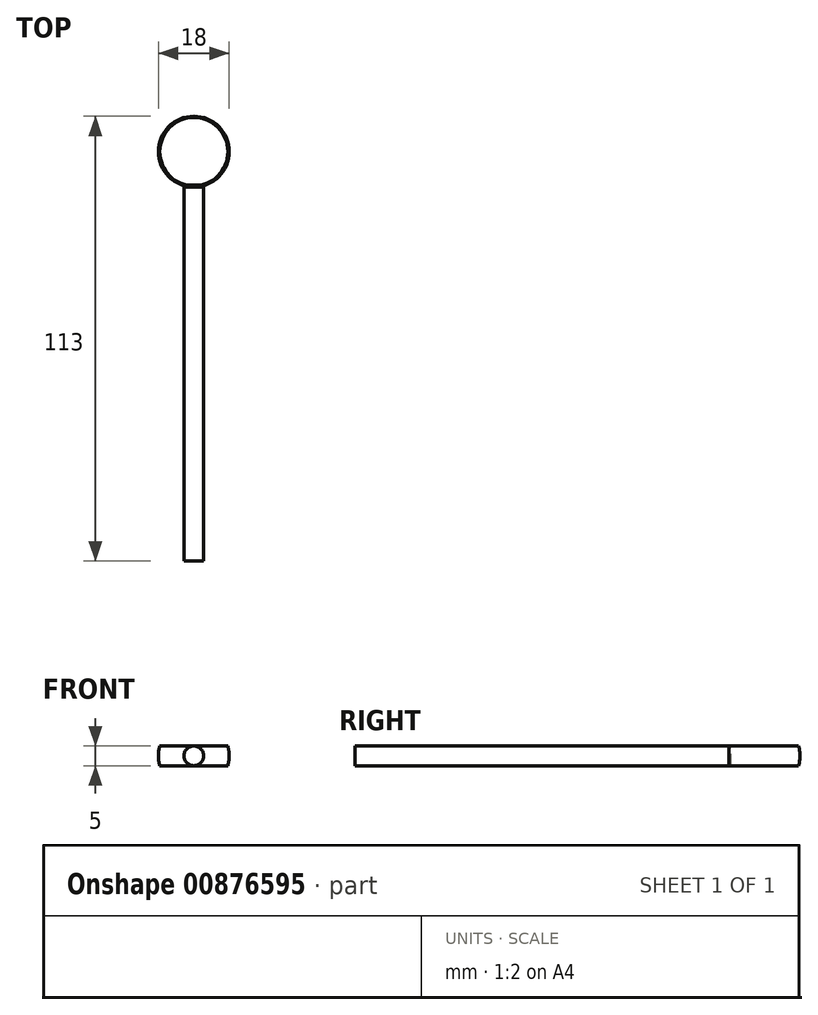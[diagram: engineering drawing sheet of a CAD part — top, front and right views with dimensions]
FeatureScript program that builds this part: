
annotation { "Feature Type Name" : "Feature", "Feature Type Description" : "" }
export const myFeature = defineFeature(function(context is Context, id is Id, definition is map)
    precondition{}
    {
        {
            var Q0;
            Q0=qCreatedBy(makeId("Front.planeOp"),FACE);
            var sketch = newSketch(context, id + "F0", { "sketchPlane" : qUnion([Q0])});
            skCircle(sketch, "E0", {"center": v(0, 0) * mm, "radius": 2.5 * mm});
            skLineSegment(sketch, "E1", {"start": v(0, 2.5) * mm, "end": v(0, -2.5) * mm});
            skSolve(sketch);
        }
        {
            var Q0;
            Q0=makeQuery(id+"F0.imprint","IMPRINT",FACE,{"disambiguationData":[TD([[makeQuery(id+"F0.imprint","IMPRINT",EDGE,{"derivedFrom":sQuery(id+"F0.wireOp",EDGE,"E0")}),1.0]])]});
            extrude(context, id + "F1", {"entities" : qUnion([Q0]), "depth" : 95 * mm, "offsetDistance" : 25 * mm});
        }
        {
            var Q0;
            Q0=sQuery(id+"F0.wireOp",EDGE,"E1");
            extrude(context, id + "F2", {"bodyType" : ToolBodyType.SURFACE, "surfaceEntities" : qUnion([Q0]), "oppositeDirection" : true, "depth" : 9 * mm, "offsetDistance" : 25 * mm});
        }
        {
            var Q0;
            Q0=makeQuery(id+"F2.opExtrude","SWEPT_FACE",FACE,{"disambiguationData":[OSD([sQuery(id+"F0.wireOp",EDGE,"E1")])]});
            var sketch = newSketch(context, id + "F3", { "sketchPlane" : qUnion([Q0])});
            skCircle(sketch, "E2", {"center": v(9, 0) * mm, "radius": 9 * mm});
            skLineSegment(sketch, "E3", {"start": v(9, 0) * mm, "end": v(9, 9) * mm});
            skLineSegment(sketch, "E4", {"start": v(9, 0) * mm, "end": v(9, -9) * mm});
            skLineSegment(sketch, "E5", {"start": v(9, 9) * mm, "end": v(9, -9) * mm});
            skSolve(sketch);
        }
        {
            var Q0;
            {var subQ0=sQuery(id+"F3.wireOp",EDGE,"E5");var subQ1=sQuery(id+"F3.wireOp",EDGE,"E2");var subQ2=makeQuery(id+"F3.imprint","INTERSECT",VERTEX,{"disambiguationData":[OD(0.0)],"derivedFrom":[subQ1,subQ0]});Q0=makeQuery(id+"F3.imprint","IMPRINT",FACE,{"disambiguationData":[TD([[makeQuery(id+"F3.imprint","IMPRINT",EDGE,{"disambiguationData":[TD([[subQ2,1.0]])],"derivedFrom":subQ1}),1.0]])]});}
            var Q1;
            Q1=sQuery(id+"F3.wireOp",EDGE,"E2");
            var Q2;
            Q2=sQuery(id+"F3.wireOp",EDGE,"E5");
            revolve(context, id + "F4", {"surfaceOperationType" : NewSurfaceOperationType.NEW, "entities" : qUnion([Q0]), "surfaceEntities" : qUnion([Q1]), "axis" : qUnion([Q2]), "revolveType" : RevolveType.FULL});
        }
        {
            var Q0;
            Q0=makeQuery(id+"F1.opExtrude","CAP_FACE",FACE,{"disambiguationData":[OSD([sQuery(id+"F0.wireOp",EDGE,"E0")])],"isStart":true});
            extrude(context, id + "F5", {"entities" : qUnion([Q0]), "depth" : 0.5 * mm, "offsetDistance" : 25 * mm});
        }
    });
